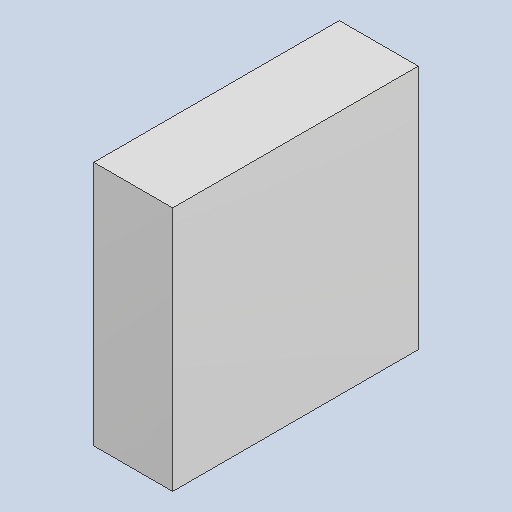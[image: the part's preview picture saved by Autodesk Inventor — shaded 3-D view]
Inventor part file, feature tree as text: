
AUTODESK INVENTOR PART (.ipt)
format: ipt  version: 2023.4 (Build 274418000, 418)  size: 81,408 bytes
history: native  units: mm
features: extrude x1
ambient origin geometry x8: Origin, YZ Plane, XZ Plane, XY Plane, X Axis, Y Axis, Z Axis, Center Point
bodies: Solid1 (feature_tree)
feature tree (1):
  extrude  "Extruded_13"  [1 undecoded]
note: 1 required parameter value undecoded (feature->parameter linkage not recoverable at this tier; creation-order binding heuristic only, values carry confidence <= 0.55)
